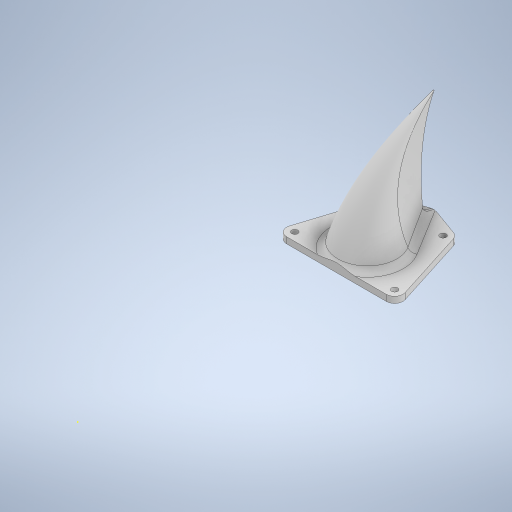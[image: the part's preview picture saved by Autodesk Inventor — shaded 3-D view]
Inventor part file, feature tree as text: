
AUTODESK INVENTOR PART (.ipt)
format: ipt  version: 2023 (Build 270158000, 158)  size: 429,056 bytes
history: native  units: in
note: dims shown in document units (in); Inventor stores cm internally (conversion verified against a paired STEP export)
features: sketch x6, plane x2, extrude x1, loft x1, fillet x1
ambient origin geometry x8: Origin, YZ Plane, XZ Plane, XY Plane, X Axis, Y Axis, Z Axis, Center Point
bodies: Solid1 (feature_tree)
feature tree (11):
  extrude  "Extrusion1"  Depth=0.1181in TaperAngle=0.0deg
  sketch  "Sketch2"  dims[d3=1.9685in d4=0.5906in d11=0.9843in]
  sketch  "Sketch3"  dims[d12=0.2953in]
  plane  "Work Plane1"
  sketch  "Sketch4"  dims[d21=0.0197in]
  plane  "Work Plane2"
  loft  "Loft3"
  fillet  "Fillet1"  Radius=0.9843in
  sketch  "Sketch6"  dims[d24=0.0in d25=90.0deg d26=0.0in d27=90.0deg d28=0.1339in]
  sketch  "Sketch1"  dims[d0=0.1181in d1=0.1181in d2=0.0in]
  sketch  "Sketch5"  dims[d22=0.0in d23=90.0deg]
